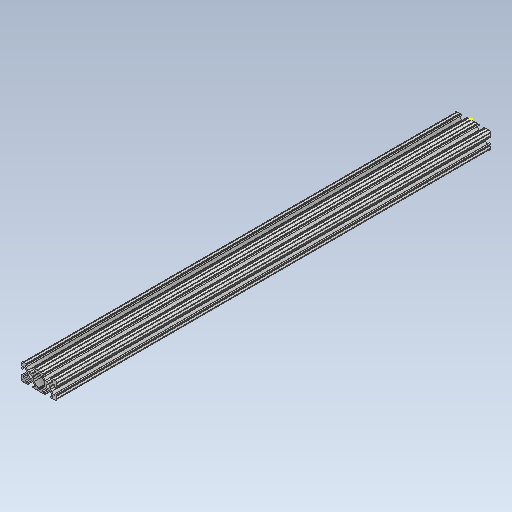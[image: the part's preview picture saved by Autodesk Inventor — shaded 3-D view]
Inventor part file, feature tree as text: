
AUTODESK INVENTOR PART (.ipt)
format: ipt  version: 2020 (Build 240168000, 168)  size: 335,872 bytes
history: native  units: in
note: dims shown in document units (in); Inventor stores cm internally (conversion verified against a paired STEP export)
features: sketch x2, extrude x1
ambient origin geometry x8: Origin, YZ Plane, XZ Plane, XY Plane, X Axis, Y Axis, Z Axis, Center Point
bodies: Solid1 (feature_tree)
feature tree (3):
  extrude  "Extrusion1"  [1 undecoded]
  sketch  "Sketch2"
  sketch  "Sketch1"  dims[d0=25.0in d1=0.0in]
note: 1 required parameter value undecoded (feature->parameter linkage not recoverable at this tier; creation-order binding heuristic only, values carry confidence <= 0.55)
